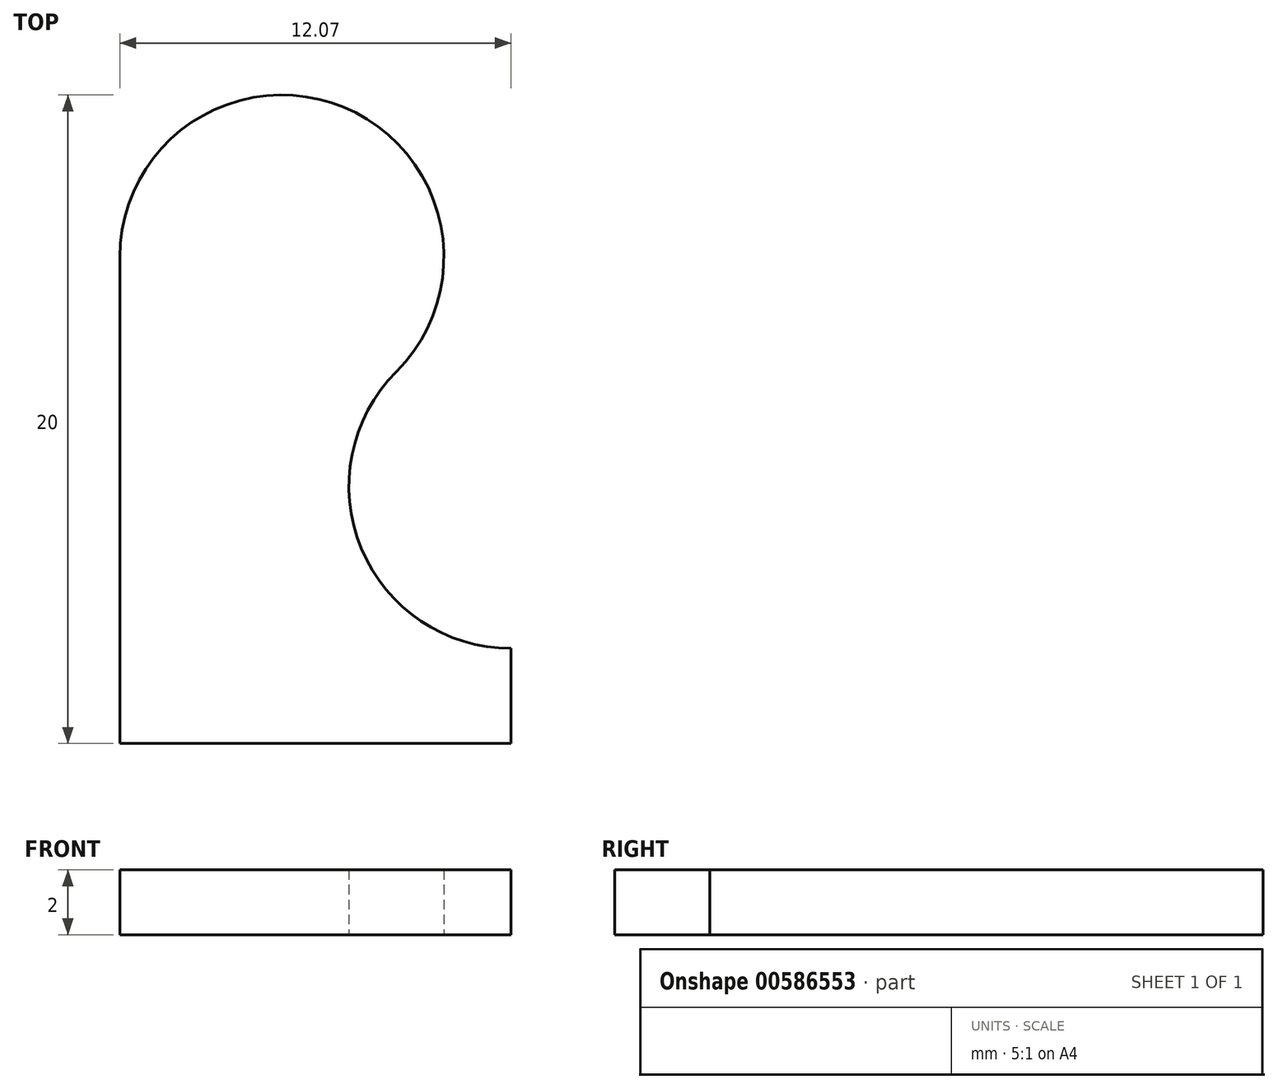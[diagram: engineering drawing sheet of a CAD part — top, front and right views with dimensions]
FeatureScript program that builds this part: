
annotation { "Feature Type Name" : "Feature", "Feature Type Description" : "" }
export const myFeature = defineFeature(function(context is Context, id is Id, definition is map)
    precondition{}
    {
        {
            var Q0;
            Q0=qCreatedBy(makeId("Top.planeOp"),FACE);
            var sketch = newSketch(context, id + "F0", { "sketchPlane" : qUnion([Q0])});
            skLineSegment(sketch, "E0", {"start": v(0, 0) * mm, "end": v(0, 15) * mm});
            skArc(sketch, "E1", {"start": v(0, 15) * mm, "mid": v(6.91, 19.62) * mm, "end": v(8.54, 11.46) * mm});
            skArc(sketch, "E2", {"start": v(8.54, 11.46) * mm, "mid": v(7.45, 6.02) * mm, "end": v(12.07, 2.93) * mm});
            skLineSegment(sketch, "E3", {"start": v(5, 15) * mm, "end": v(12.07, 7.93) * mm, "construction": true});
            skLineSegment(sketch, "E4", {"start": v(12.07, 0) * mm, "end": v(12.07, 7.93) * mm, "construction": true});
            skLineSegment(sketch, "E5", {"start": v(0, 0) * mm, "end": v(12.07, 0) * mm});
            skLineSegment(sketch, "E6", {"start": v(12.07, 2.93) * mm, "end": v(12.07, 0) * mm});
            skLineSegment(sketch, "E7", {"start": v(0, 15) * mm, "end": v(5, 15) * mm, "construction": true});
            skLineSegment(sketch, "E8", {"start": v(5, 15) * mm, "end": v(5, 10) * mm, "construction": true});
            skLineSegment(sketch, "E9", {"start": v(5, 10) * mm, "end": v(5, 5) * mm, "construction": true});
            skLineSegment(sketch, "E10", {"start": v(5, 0) * mm, "end": v(5, 5) * mm, "construction": true});
            skSolve(sketch);
        }
        {
            var Q0;
            Q0=qSketchRegion(id+"F0",true);
            extrude(context, id + "F1", {"entities" : qUnion([Q0]), "depth" : 2 * mm, "offsetDistance" : 25 * mm});
        }
    });
